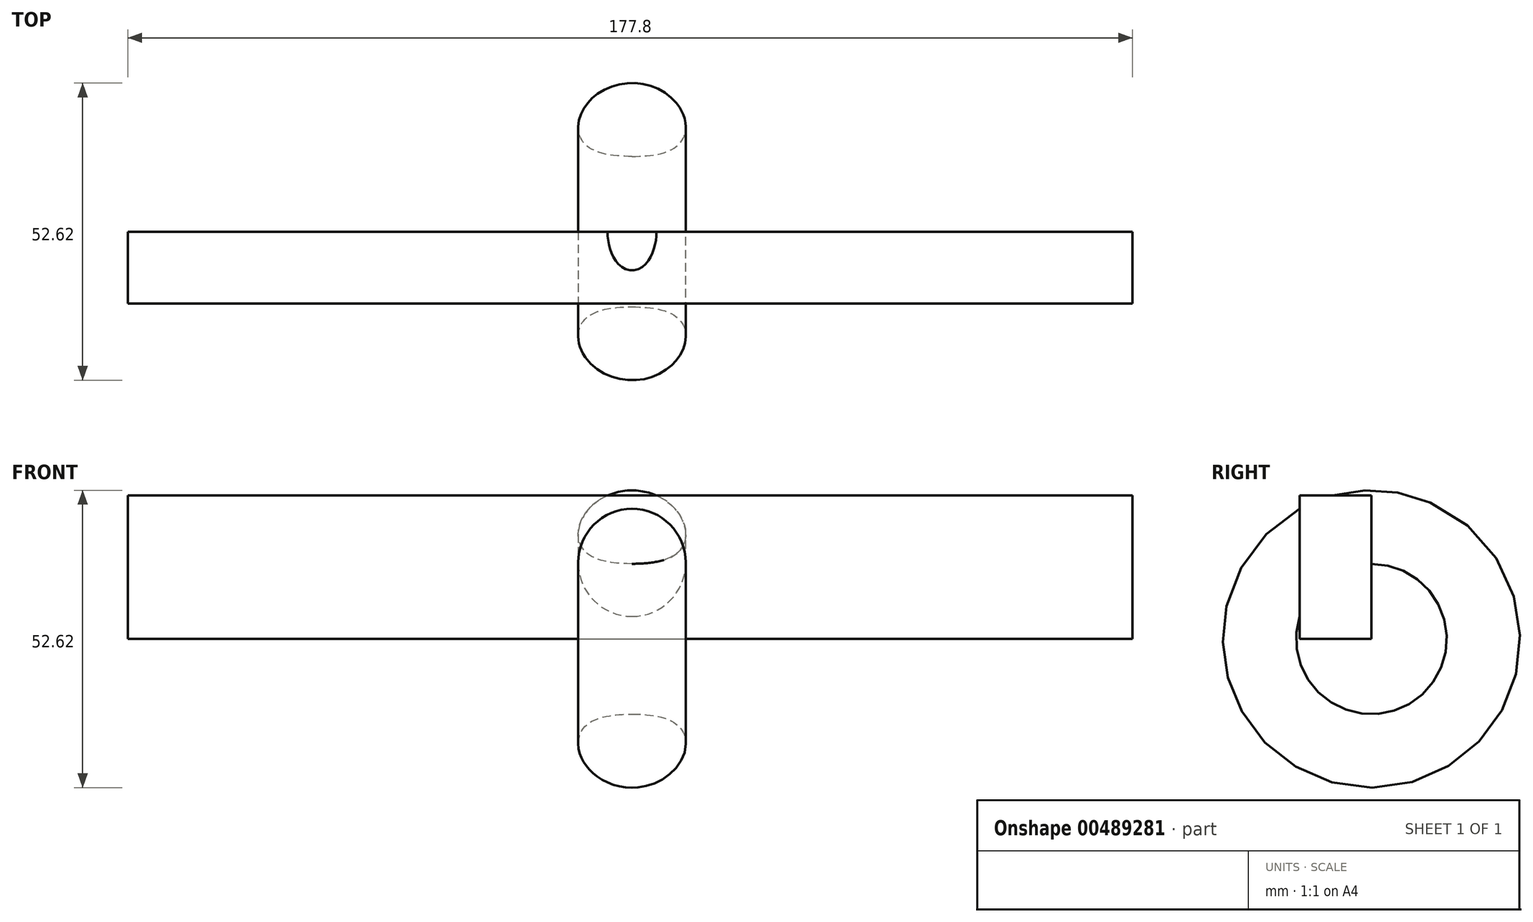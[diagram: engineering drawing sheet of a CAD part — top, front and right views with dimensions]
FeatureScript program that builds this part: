
annotation { "Feature Type Name" : "Feature", "Feature Type Description" : "" }
export const myFeature = defineFeature(function(context is Context, id is Id, definition is map)
    precondition{}
    {
        {
            var Q0;
            Q0=qCreatedBy(makeId("Front.planeOp"),FACE);
            var sketch = newSketch(context, id + "F0", { "sketchPlane" : qUnion([Q0])});
            skLineSegment(sketch, "E0.bottom", {"start": v(-185.28, -82.88) * mm, "end": v(-7.48, -82.88) * mm});
            skLineSegment(sketch, "E0.top", {"start": v(-185.28, -57.48) * mm, "end": v(-7.48, -57.48) * mm});
            skLineSegment(sketch, "E0.left", {"start": v(-185.28, -82.88) * mm, "end": v(-185.28, -57.48) * mm});
            skLineSegment(sketch, "E0.right", {"start": v(-7.48, -82.88) * mm, "end": v(-7.48, -57.48) * mm});
            skSolve(sketch);
        }
        {
            var Q0;
            Q0 = qSketchRegion(id + "F0", true);
            extrude(context, id + "F1", {"entities" : qUnion([Q0]), "endBound" : BoundingType.SYMMETRIC, "depth" : 12.7 * mm});
        }
        {
            var Q0;
            Q0=makeQuery(id+"F1.opExtrude","CAP_FACE",FACE,{"disambiguationData":[OSD([sQuery(id+"F0.wireOp",EDGE,"E0.bottom"),sQuery(id+"F0.wireOp",EDGE,"E0.top"),sQuery(id+"F0.wireOp",EDGE,"E0.left"),sQuery(id+"F0.wireOp",EDGE,"E0.right")])],"isStart":false});
            var sketch = newSketch(context, id + "F2", { "sketchPlane" : qUnion([Q0])});
            skCircle(sketch, "E1", {"center": v(-96.05, -69.36) * mm, "radius": 9.52 * mm});
            skSolve(sketch);
        }
        {
            var Q0;
            Q0=makeQuery(id+"F2.imprint","IMPRINT",FACE,{"disambiguationData":[TD([[makeQuery(id+"F2.imprint","IMPRINT",EDGE,{"derivedFrom":sQuery(id+"F2.wireOp",EDGE,"E1")}),1.0]])]});
            var Q1;
            Q1=makeQuery(id+"F1.opExtrude","CAP_EDGE",EDGE,{"disambiguationData":[OSD([sQuery(id+"F0.wireOp",EDGE,"E0.bottom")])],"isStart":true});
            revolve(context, id + "F3", {"operationType" : NewBodyOperationType.ADD, "entities" : qUnion([Q0]), "axis" : qUnion([Q1]), "revolveType" : RevolveType.FULL});
        }
    });
